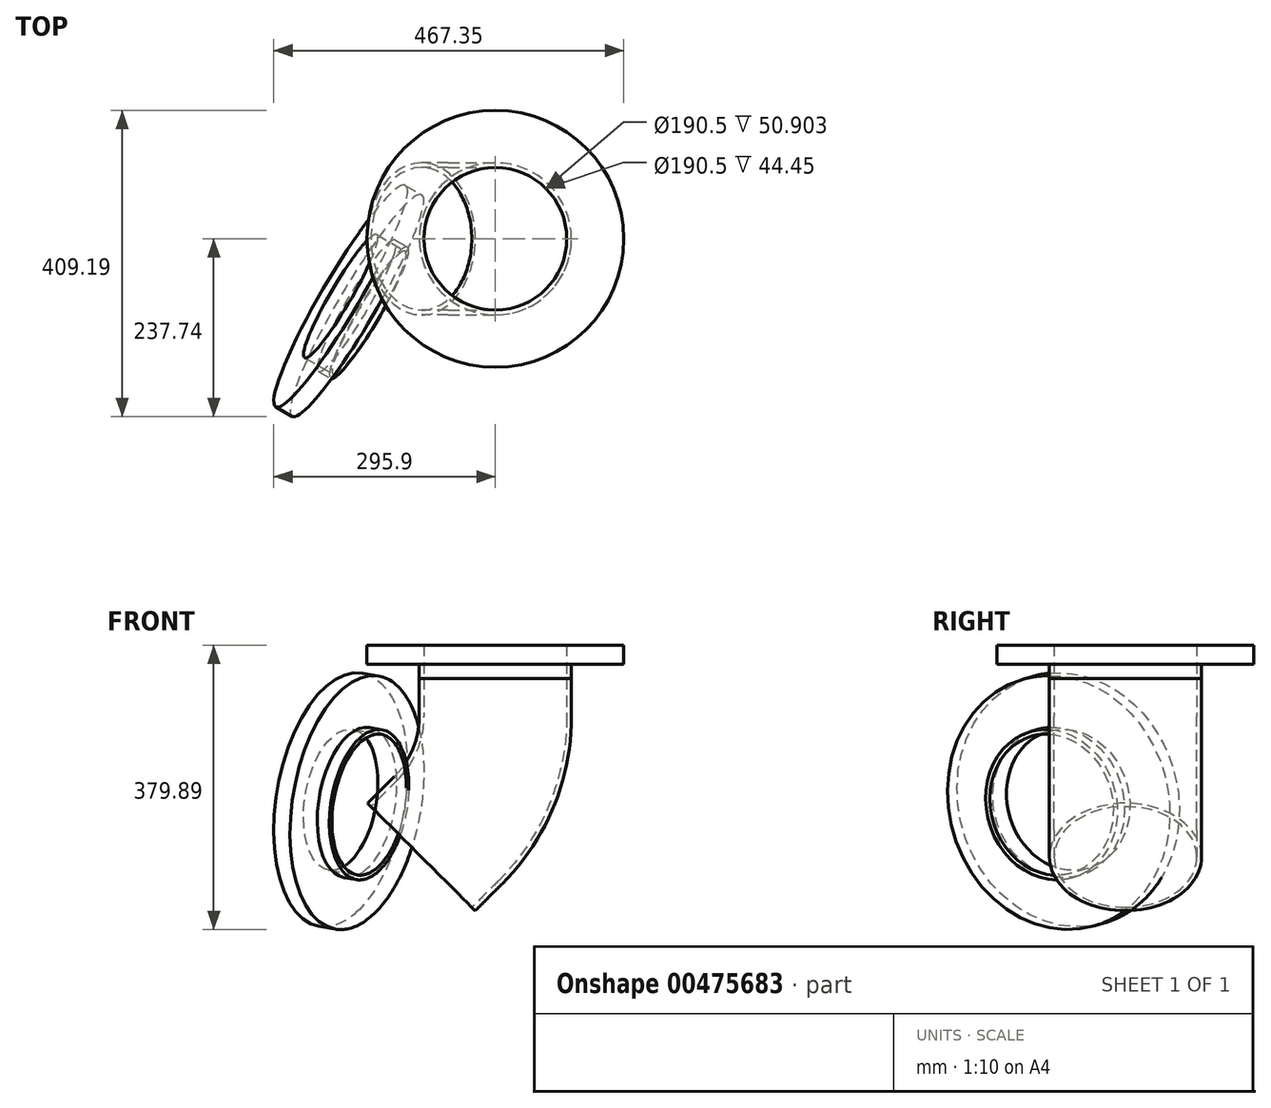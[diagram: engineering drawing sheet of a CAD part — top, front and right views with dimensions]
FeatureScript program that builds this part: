
annotation { "Feature Type Name" : "Feature", "Feature Type Description" : "" }
export const myFeature = defineFeature(function(context is Context, id is Id, definition is map)
    precondition{}
    {
        {
            var Q0;
            Q0=qCreatedBy(makeId("Top.planeOp"),FACE);
            var sketch = newSketch(context, id + "F0", { "sketchPlane" : qUnion([Q0])});
            skCircle(sketch, "E0", {"center": v(0, 0) * mm, "radius": 95.25 * mm});
            skCircle(sketch, "E1", {"center": v(0, 0) * mm, "radius": 101.6 * mm});
            skSolve(sketch);
        }
        {
            var Q0;
            Q0=makeQuery(id+"F0.imprint","IMPRINT",FACE,{"disambiguationData":[TD([[makeQuery(id+"F0.imprint","IMPRINT",EDGE,{"derivedFrom":sQuery(id+"F0.wireOp",EDGE,"E0")}),-1.0]])]});
            extrude(context, id + "F1", {"entities" : qUnion([Q0]), "depth" : 19.05 * mm});
        }
        {
            var Q0;
            Q0=makeQuery(id+"F1.opExtrude","CAP_FACE",FACE,{"disambiguationData":[OSD([sQuery(id+"F0.wireOp",EDGE,"E0"),sQuery(id+"F0.wireOp",EDGE,"E1")])],"isStart":false});
            var sketch = newSketch(context, id + "F2", { "sketchPlane" : qUnion([Q0])});
            skCircle(sketch, "E2", {"center": v(0, 0) * mm, "radius": 171.45 * mm});
            skSolve(sketch);
        }
        {
            var Q0;
            Q0=makeQuery(id+"F2.imprint","IMPRINT",FACE,{"disambiguationData":[TD([[makeQuery(id+"F2.imprint","IMPRINT",EDGE,{"derivedFrom":sQuery(id+"F2.wireOp",EDGE,"E2")}),1.0]])]});
            var Q1;
            Q1=makeQuery(id+"F2.imprint","IMPRINT",FACE,{"disambiguationData":[TD([[makeQuery(id+"F2.imprint","IMPRINT",EDGE,{"derivedFrom":makeQuery(id+"F1.opExtrude","CAP_EDGE",EDGE,{"disambiguationData":[OSD([sQuery(id+"F0.wireOp",EDGE,"E0")])],"isStart":false})}),-1.0]])]});
            extrude(context, id + "F3", {"entities" : qUnion([Q0, Q1]), "operationType" : NewBodyOperationType.ADD, "depth" : 25.4 * mm});
        }
        {
            var Q0;
            Q0=qCreatedBy(makeId("Front.planeOp"),FACE);
            var sketch = newSketch(context, id + "F4", { "sketchPlane" : qUnion([Q0])});
            skLineSegment(sketch, "E3", {"start": v(0, 0) * mm, "end": v(0, -50.9) * mm});
            skLineSegment(sketch, "E4", {"start": v(-62.79, -202.49) * mm, "end": v(-98.78, -238.48) * mm});
            skPoint(sketch, "E5.visualSharp", {"position": v(0, -139.7) * mm});
            skArc(sketch, "E5.filletArc", {"start": v(-62.79, -202.49) * mm, "mid": v(-16.32, -132.94) * mm, "end": v(0, -50.9) * mm});
            skSolve(sketch);
        }
        {
            var Q0;
            Q0=makeQuery(id+"F1.opExtrude","CAP_FACE",FACE,{"disambiguationData":[OSD([sQuery(id+"F0.wireOp",EDGE,"E0"),sQuery(id+"F0.wireOp",EDGE,"E1")])],"isStart":true});
            var Q1;
            Q1=sQuery(id+"F4.wireOp",EDGE,"E5.filletArc");
            var Q2;
            Q2=sQuery(id+"F4.wireOp",EDGE,"E4");
            var Q3;
            Q3=sQuery(id+"F4.wireOp",EDGE,"E3");
            sweep(context, id + "F5", {"profiles" : qUnion([Q0]), "path" : qUnion([Q1, Q2, Q3])});
        }
        {
            var Q0;
            Q0=makeQuery(id+"F5.opSweep","CAP_FACE",FACE,{"disambiguationData":[OSD([sQuery(id+"F0.wireOp",EDGE,"E0"),sQuery(id+"F0.wireOp",EDGE,"E1"),sQuery(id+"F4.wireOp",VERTEX,"E4.end")])],"isStart":false});
            var sketch = newSketch(context, id + "F6", { "sketchPlane" : qUnion([Q0])});
            skPoint(sketch, "E6", {"position": v(98.78, 0) * mm});
            skLineSegment(sketch, "E7", {"start": v(98.78, 0) * mm, "end": v(98.78, 343.85) * mm, "construction": true});
            skSolve(sketch);
        }
        {
            var Q0;
            Q0=makeQuery(id+"F1.opExtrude","SWEPT_BODY",BODY,{"disambiguationData":[OSD([sQuery(id+"F0.wireOp",EDGE,"E0"),sQuery(id+"F0.wireOp",EDGE,"E1")])]});
            var Q1;
            Q1=qCreatedBy(makeId("Origin.pointOp"),VERTEX);
            var Q2;
            Q2=sQuery(id+"F6.wireOp",VERTEX,"E6");
            transform(context, id + "F7", {"entities" : qUnion([Q0]), "transformType" : TransformType.TRANSLATION_ENTITY, "oppositeDirectionEntity" : false, "transformLine" : qUnion([Q1, Q2]), "makeCopy" : true});
        }
        {
            var Q0;
            Q0=makeQuery(id+"F7.opPattern","COPY",BODY,{"derivedFrom":makeQuery(id+"F1.opExtrude","SWEPT_BODY",BODY,{"disambiguationData":[OSD([sQuery(id+"F0.wireOp",EDGE,"E0"),sQuery(id+"F0.wireOp",EDGE,"E1")])]}),"instanceName":"1"});
            var Q1;
            Q1=sQuery(id+"F6.wireOp",VERTEX,"E6");
            var Q2;
            Q2=sQuery(id+"F6.wireOp",EDGE,"E7");
            transform(context, id + "F8", {"entities" : qUnion([Q0]), "transformType" : TransformType.ROTATION, "transformAxis" : qUnion([Q2]), "angle" : 135 * degree, "makeCopy" : false});
        }
    });
